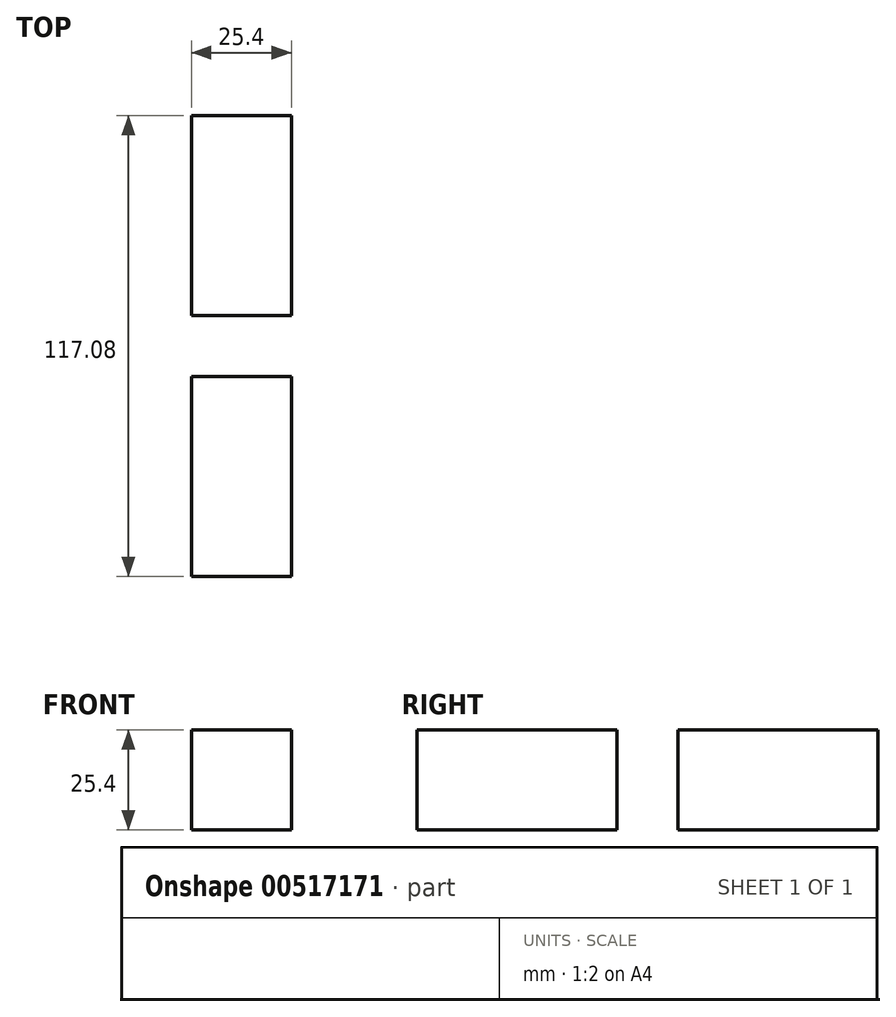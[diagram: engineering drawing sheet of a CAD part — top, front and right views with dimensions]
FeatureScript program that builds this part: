
annotation { "Feature Type Name" : "Feature", "Feature Type Description" : "" }
export const myFeature = defineFeature(function(context is Context, id is Id, definition is map)
    precondition{}
    {
        {
            var Q0;
            Q0=qCreatedBy(makeId("Top.planeOp"),FACE);
            var sketch = newSketch(context, id + "F0", { "sketchPlane" : qUnion([Q0])});
            skLineSegment(sketch, "E0.bottom", {"start": v(-18.21, 58.54) * mm, "end": v(7.19, 58.54) * mm});
            skLineSegment(sketch, "E0.top", {"start": v(-18.21, 7.74) * mm, "end": v(7.19, 7.74) * mm});
            skLineSegment(sketch, "E0.left", {"start": v(-18.21, 58.54) * mm, "end": v(-18.21, 7.74) * mm});
            skLineSegment(sketch, "E0.right", {"start": v(7.19, 58.54) * mm, "end": v(7.19, 7.74) * mm});
            skLineSegment(sketch, "E1", {"start": v(-71.71, 0) * mm, "end": v(62.5, 0) * mm, "construction": true});
            skLineSegment(sketch, "E2.MirrorCS", {"start": v(-18.21, -7.74) * mm, "end": v(7.19, -7.74) * mm});
            skLineSegment(sketch, "E3.MirrorCS", {"start": v(7.19, -58.54) * mm, "end": v(7.19, -7.74) * mm});
            skLineSegment(sketch, "E4.MirrorCS", {"start": v(-18.21, -58.54) * mm, "end": v(7.19, -58.54) * mm});
            skLineSegment(sketch, "E5.MirrorCS", {"start": v(-18.21, -58.54) * mm, "end": v(-18.21, -7.74) * mm});
            skSolve(sketch);
        }
        {
            var Q0;
            Q0=makeQuery(id+"F0.imprint","IMPRINT",FACE,{"disambiguationData":[TD([[makeQuery(id+"F0.imprint","IMPRINT",EDGE,{"derivedFrom":sQuery(id+"F0.wireOp",EDGE,"E0.bottom")}),-1.0]])]});
            var Q1;
            Q1=makeQuery(id+"F0.imprint","IMPRINT",FACE,{"disambiguationData":[TD([[makeQuery(id+"F0.imprint","IMPRINT",EDGE,{"derivedFrom":sQuery(id+"F0.wireOp",EDGE,"E2.MirrorCS")}),-1.0]])]});
            extrude(context, id + "F1", {"entities" : qUnion([Q0, Q1]), "depth" : 25.4 * mm, "offsetDistance" : 25.4 * mm});
        }
    });
